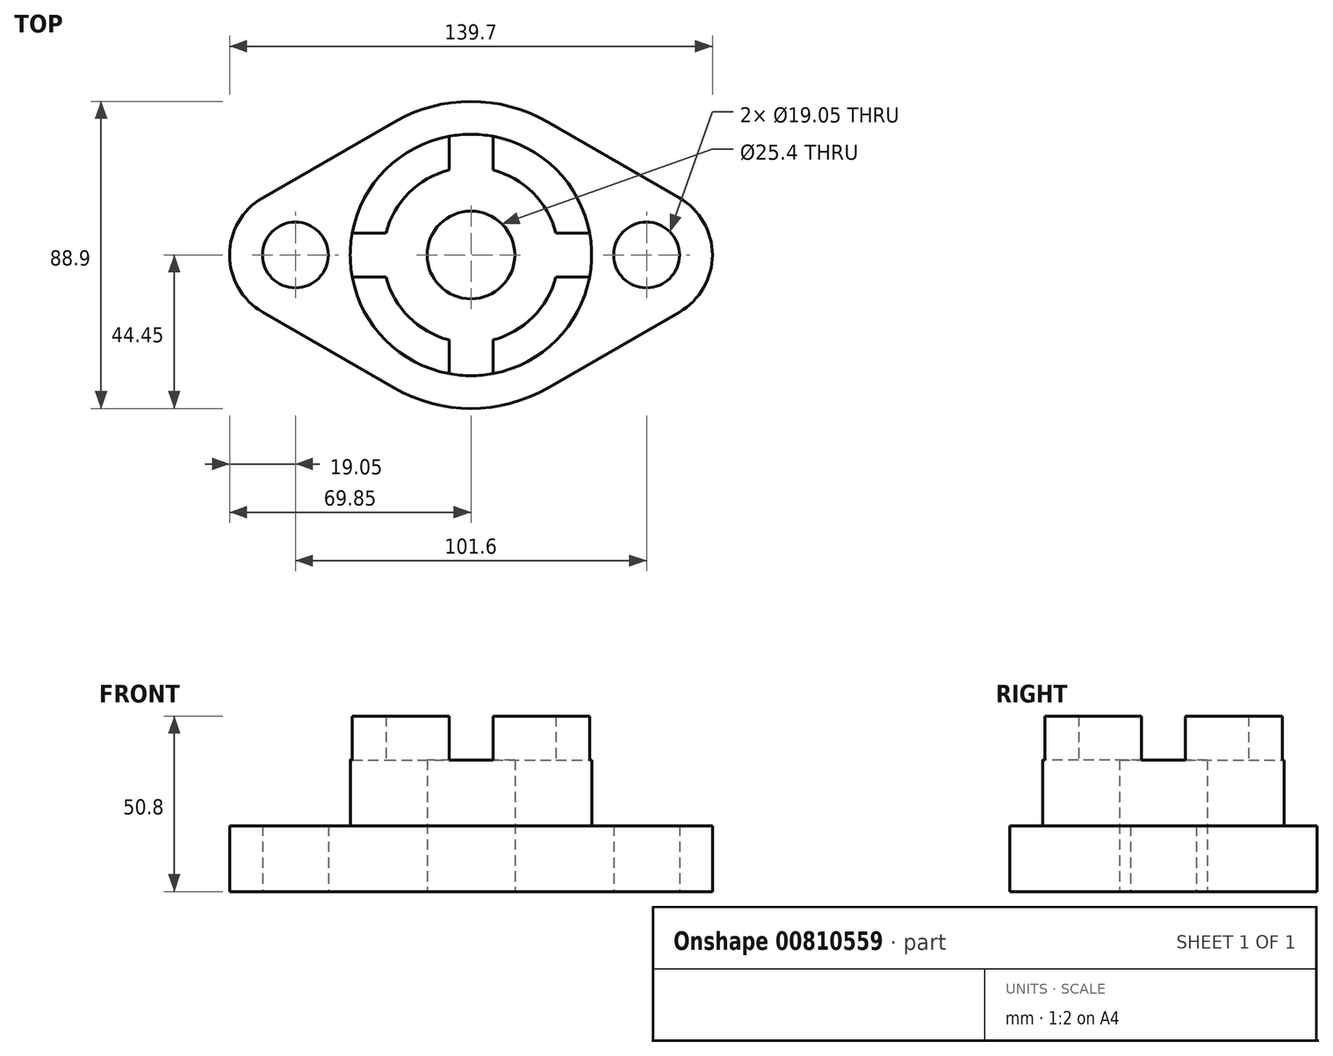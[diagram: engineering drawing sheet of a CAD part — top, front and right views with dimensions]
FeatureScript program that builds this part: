
annotation { "Feature Type Name" : "Feature", "Feature Type Description" : "" }
export const myFeature = defineFeature(function(context is Context, id is Id, definition is map)
    precondition{}
    {
        {
            var Q0;
            Q0=qCreatedBy(makeId("Top.planeOp"),FACE);
            var sketch = newSketch(context, id + "F0", { "sketchPlane" : qUnion([Q0])});
            skArc(sketch, "E0", {"start": v(-22.23, -38.5) * mm, "mid": v(0, -44.45) * mm, "end": v(22.23, -38.5) * mm});
            skCircle(sketch, "E1", {"center": v(0, 0) * mm, "radius": 34.93 * mm});
            skCircle(sketch, "E2", {"center": v(0, 0) * mm, "radius": 25.4 * mm});
            skCircle(sketch, "E3", {"center": v(0, 0) * mm, "radius": 12.7 * mm});
            skArc(sketch, "E4", {"start": v(-60.32, 16.5) * mm, "mid": v(-69.85, 0) * mm, "end": v(-60.33, -16.5) * mm});
            skArc(sketch, "E5", {"start": v(60.33, -16.5) * mm, "mid": v(69.85, 0) * mm, "end": v(60.33, 16.5) * mm});
            skLineSegment(sketch, "E6", {"start": v(-60.33, 16.5) * mm, "end": v(-22.23, 38.5) * mm});
            skLineSegment(sketch, "E7", {"start": v(22.22, 38.5) * mm, "end": v(60.33, 16.5) * mm});
            skLineSegment(sketch, "E8", {"start": v(-60.33, -16.5) * mm, "end": v(-22.22, -38.5) * mm});
            skLineSegment(sketch, "E9", {"start": v(22.22, -38.5) * mm, "end": v(60.33, -16.5) * mm});
            skArc(sketch, "E10.trimOffspring", {"start": v(22.22, 38.5) * mm, "mid": v(0, 44.45) * mm, "end": v(-22.23, 38.5) * mm});
            skCircle(sketch, "E11", {"center": v(-50.8, 0) * mm, "radius": 9.53 * mm});
            skCircle(sketch, "E12", {"center": v(50.8, 0) * mm, "radius": 9.53 * mm});
            skPoint(sketch, "E13.orphan", {"position": v(-12.7, 0) * mm});
            skPoint(sketch, "E14.orphan", {"position": v(12.7, 0) * mm});
            skLineSegment(sketch, "E15", {"start": v(-6.35, -24.6) * mm, "end": v(-6.35, -34.34) * mm});
            skLineSegment(sketch, "E16", {"start": v(6.35, -24.6) * mm, "end": v(6.35, -34.34) * mm});
            skLineSegment(sketch, "E17", {"start": v(-34.34, 6.35) * mm, "end": v(-24.6, 6.35) * mm});
            skLineSegment(sketch, "E18", {"start": v(-24.6, -6.35) * mm, "end": v(-34.34, -6.35) * mm});
            skLineSegment(sketch, "E19", {"start": v(-6.35, 34.34) * mm, "end": v(-6.35, 24.6) * mm});
            skLineSegment(sketch, "E20", {"start": v(6.35, 24.6) * mm, "end": v(6.35, 34.34) * mm});
            skLineSegment(sketch, "E21", {"start": v(24.6, 6.35) * mm, "end": v(34.34, 6.35) * mm});
            skLineSegment(sketch, "E22", {"start": v(24.6, -6.35) * mm, "end": v(34.34, -6.35) * mm});
            skSolve(sketch);
        }
        {
            var Q0;
            Q0=makeQuery(id+"F0.imprint","IMPRINT",FACE,{"disambiguationData":[TD([[makeQuery(id+"F0.imprint","IMPRINT",EDGE,{"derivedFrom":sQuery(id+"F0.wireOp",EDGE,"E0")}),1.0]])]});
            extrude(context, id + "F1", {"entities" : qUnion([Q0]), "depth" : 19.05 * mm, "offsetDistance" : 25.4 * mm});
        }
        {
            var Q0;
            Q0=makeQuery(id+"F0.imprint","IMPRINT",FACE,{"disambiguationData":[TD([[makeQuery(id+"F0.imprint","IMPRINT",EDGE,{"derivedFrom":sQuery(id+"F0.wireOp",EDGE,"E3")}),-1.0]])]});
            var Q1;
            {var subQ0=sQuery(id+"F0.wireOp",EDGE,"E17");Q1=makeQuery(id+"F0.imprint","IMPRINT",FACE,{"disambiguationData":[TD([[makeQuery(id+"F0.imprint","IMPRINT",EDGE,{"derivedFrom":subQ0}),-1.0]])]});}
            var Q2;
            {var subQ0=sQuery(id+"F0.wireOp",EDGE,"E19");Q2=makeQuery(id+"F0.imprint","IMPRINT",FACE,{"disambiguationData":[TD([[makeQuery(id+"F0.imprint","IMPRINT",EDGE,{"derivedFrom":subQ0}),1.0]])]});}
            var Q3;
            {var subQ0=sQuery(id+"F0.wireOp",EDGE,"E15");Q3=makeQuery(id+"F0.imprint","IMPRINT",FACE,{"disambiguationData":[TD([[makeQuery(id+"F0.imprint","IMPRINT",EDGE,{"derivedFrom":subQ0}),1.0]])]});}
            var Q4;
            {var subQ0=sQuery(id+"F0.wireOp",EDGE,"E21");Q4=makeQuery(id+"F0.imprint","IMPRINT",FACE,{"disambiguationData":[TD([[makeQuery(id+"F0.imprint","IMPRINT",EDGE,{"derivedFrom":subQ0}),-1.0]])]});}
            extrude(context, id + "F2", {"entities" : qUnion([Q0, Q1, Q2, Q3, Q4]), "operationType" : NewBodyOperationType.ADD, "depth" : 38.1 * mm, "offsetDistance" : 25.4 * mm});
        }
        {
            var Q0;
            {var subQ0=sQuery(id+"F0.wireOp",EDGE,"E20");Q0=makeQuery(id+"F0.imprint","IMPRINT",FACE,{"disambiguationData":[TD([[makeQuery(id+"F0.imprint","IMPRINT",EDGE,{"derivedFrom":subQ0}),-1.0]])]});}
            var Q1;
            {var subQ0=sQuery(id+"F0.wireOp",EDGE,"E16");Q1=makeQuery(id+"F0.imprint","IMPRINT",FACE,{"disambiguationData":[TD([[makeQuery(id+"F0.imprint","IMPRINT",EDGE,{"derivedFrom":subQ0}),1.0]])]});}
            var Q2;
            {var subQ0=sQuery(id+"F0.wireOp",EDGE,"E15");Q2=makeQuery(id+"F0.imprint","IMPRINT",FACE,{"disambiguationData":[TD([[makeQuery(id+"F0.imprint","IMPRINT",EDGE,{"derivedFrom":subQ0}),-1.0]])]});}
            var Q3;
            {var subQ0=sQuery(id+"F0.wireOp",EDGE,"E17");Q3=makeQuery(id+"F0.imprint","IMPRINT",FACE,{"disambiguationData":[TD([[makeQuery(id+"F0.imprint","IMPRINT",EDGE,{"derivedFrom":subQ0}),1.0]])]});}
            extrude(context, id + "F3", {"entities" : qUnion([Q0, Q1, Q2, Q3]), "operationType" : NewBodyOperationType.ADD, "depth" : 50.8 * mm, "offsetDistance" : 25.4 * mm});
        }
    });
